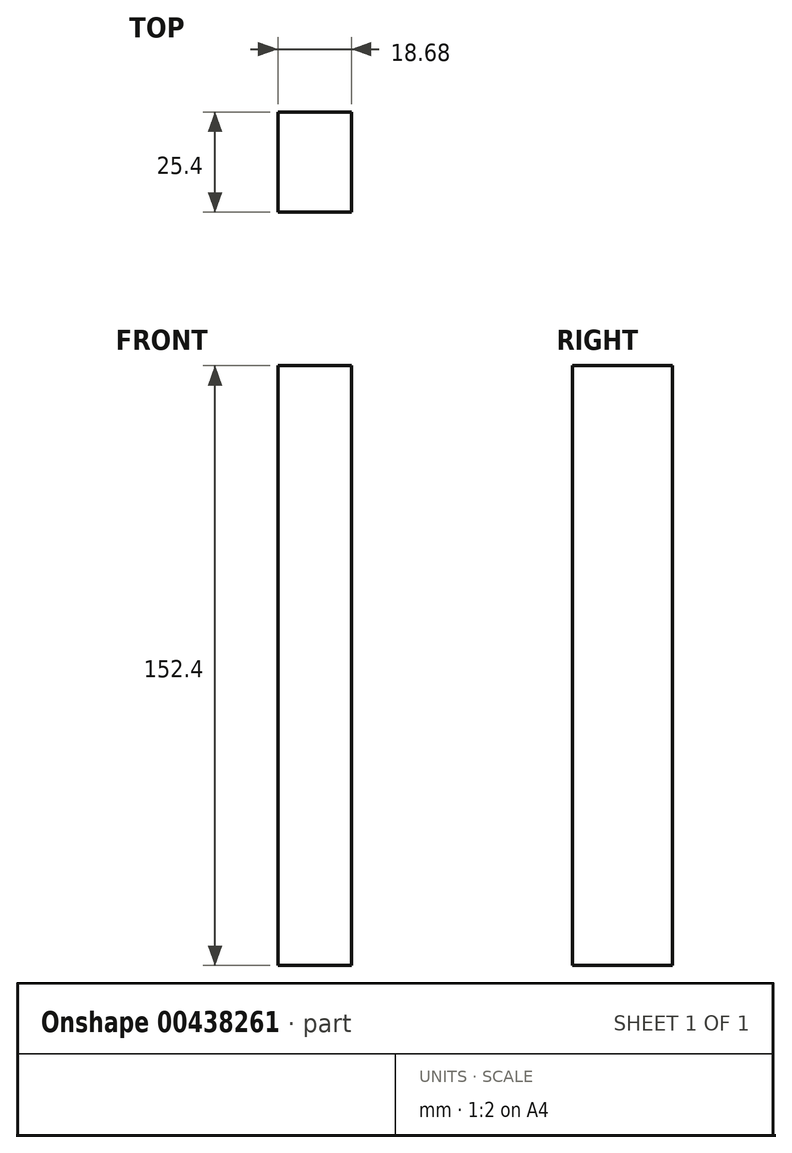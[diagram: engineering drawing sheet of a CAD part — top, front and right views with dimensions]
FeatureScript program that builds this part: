
annotation { "Feature Type Name" : "Feature", "Feature Type Description" : "" }
export const myFeature = defineFeature(function(context is Context, id is Id, definition is map)
    precondition{}
    {
        {
            var Q0;
            Q0=qCreatedBy(makeId("Front.planeOp"),FACE);
            var sketch = newSketch(context, id + "F0", { "sketchPlane" : qUnion([Q0])});
            skLineSegment(sketch, "E0.bottom", {"start": v(26.33, 92.36) * mm, "end": v(45, 92.36) * mm});
            skLineSegment(sketch, "E0.top", {"start": v(26.33, -60.04) * mm, "end": v(45, -60.04) * mm});
            skLineSegment(sketch, "E0.left", {"start": v(26.33, 92.36) * mm, "end": v(26.33, -60.04) * mm});
            skLineSegment(sketch, "E0.right", {"start": v(45, 92.36) * mm, "end": v(45, -60.04) * mm});
            skSolve(sketch);
        }
        {
            var Q0;
            Q0 = qSketchRegion(id + "F0", true);
            extrude(context, id + "F1", {"entities" : qUnion([Q0]), "depth" : 25.4 * mm});
        }
    });
